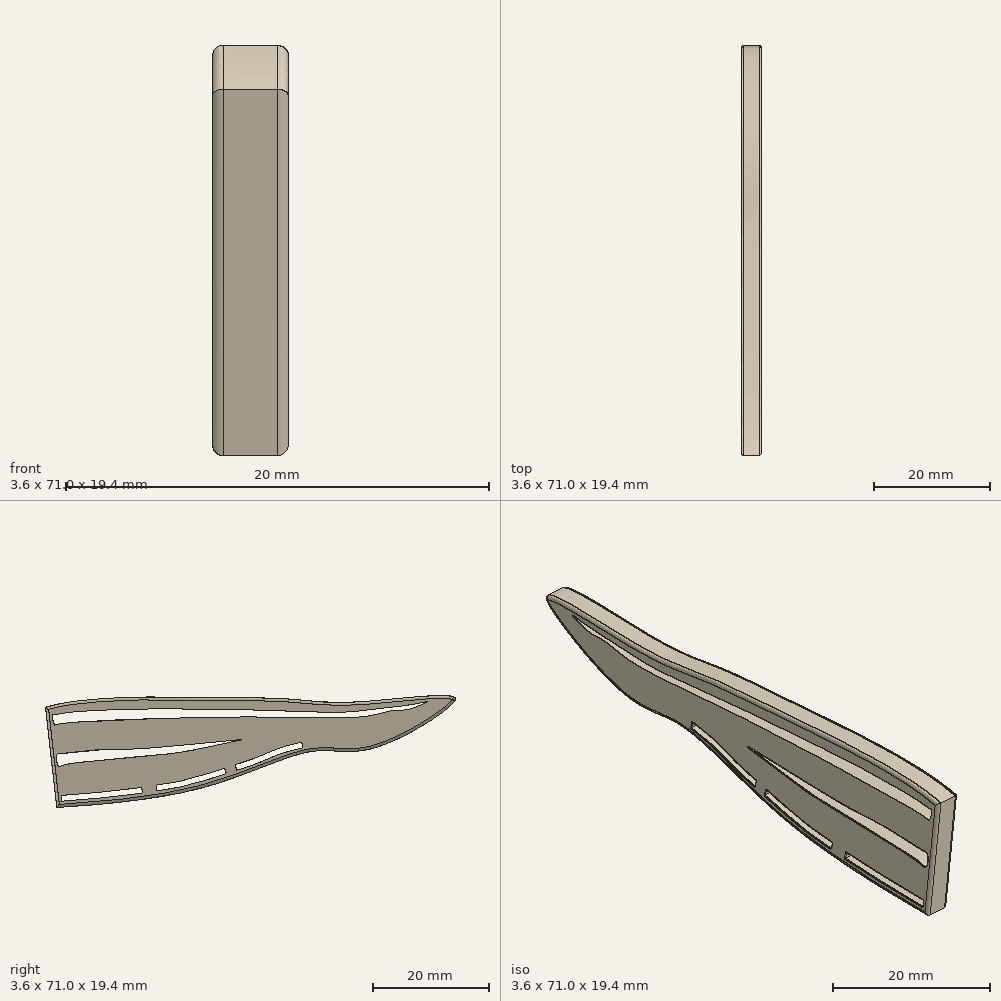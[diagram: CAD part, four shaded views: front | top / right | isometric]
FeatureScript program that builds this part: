
annotation { "Feature Type Name" : "Feature", "Feature Type Description" : "" }
export const myFeature = defineFeature(function(context is Context, id is Id, definition is map)
    precondition{}
    {
        {
            var Q0;
            Q0=qCreatedBy(makeId("Right.planeOp"),FACE);
            var sketch = newSketch(context, id + "F0", { "sketchPlane" : qUnion([Q0])});
            skFitSpline(sketch, "E0", {"points": [v(-65.8, 42.64) * mm, v(-54.6, 44.06) * mm, v(-40.36, 44.06) * mm, v(-30.2, 43.82) * mm, v(-21.14, 43.4) * mm, v(-6.78, 44.06) * mm, v(-8.12, 42.17) * mm, v(-19.19, 36.55) * mm, v(-26.3, 36.4) * mm, v(-32.36, 34.82) * mm, v(-37.4, 32.89) * mm, v(-44.89, 30.58) * mm, v(-64.17, 28.2) * mm], "startDerivative": vector(96.7, 29.58) * mm, "endDerivative": vector(-199.88, -11.49) * mm});
            skLineSegment(sketch, "E1", {"start": v(-65.8, 42.64) * mm, "end": v(-64.17, 28.2) * mm});
            skSolve(sketch);
        }
        {
            var Q0;
            Q0 = qSketchRegion(id + "F0", true);
            extrude(context, id + "F1", {"entities" : qUnion([Q0]), "depth" : 3 * mm, "offsetDistance" : 25 * mm});
        }
        {
            var Q0;
            Q0=makeQuery(id+"F1.opExtrude","SWEPT_BODY",BODY,{"disambiguationData":[OSD([sQuery(id+"F0.wireOp",EDGE,"E0"),sQuery(id+"F0.wireOp",EDGE,"E1")])]});
            var Q1;
            Q1=makeQuery(id+"F1.opExtrude","CAP_EDGE",EDGE,{"disambiguationData":[OSD([sQuery(id+"F0.wireOp",EDGE,"E1")])],"isStart":false});
            var Q2;
            {var subQ0=sQuery(id+"F0.wireOp",EDGE,"E1");var subQ1=sQuery(id+"F0.wireOp",EDGE,"E0");Q2=makeQuery(id+"F1.opExtrude","CAP_VERTEX",VERTEX,{"disambiguationData":[OSD([subQ1,subQ0]),TDD([makeQuery(id+"F0.imprint","INTERSECT",VERTEX,{"disambiguationData":[OD(1.0)],"derivedFrom":[subQ1,subQ0]})])],"isStart":false});}
            transform(context, id + "F2", {"entities" : qUnion([Q0]), "transformType" : TransformType.SCALE_UNIFORMLY, "scale" : 1.2, "scalePoint" : qUnion([Q2]), "makeCopy" : false});
        }
        {
            var Q0;
            Q0=makeQuery(id+"F1.opExtrude","CAP_FACE",FACE,{"disambiguationData":[OSD([sQuery(id+"F0.wireOp",EDGE,"E0"),sQuery(id+"F0.wireOp",EDGE,"E1")])],"isStart":true});
            var Q1;
            Q1=makeQuery(id+"F1.opExtrude","CAP_FACE",FACE,{"disambiguationData":[OSD([sQuery(id+"F0.wireOp",EDGE,"E0"),sQuery(id+"F0.wireOp",EDGE,"E1")])],"isStart":false});
            fillet(context, id + "F3", {"entities" : qUnion([Q0, Q1]), "radius" : 0.5 * mm, "tangentPropagation" : true, "allowEdgeOverflow" : false});
        }
        {
            var Q0;
            Q0=makeQuery(id+"F1.opExtrude","CAP_FACE",FACE,{"disambiguationData":[OSD([sQuery(id+"F0.wireOp",EDGE,"E0"),sQuery(id+"F0.wireOp",EDGE,"E1")])],"isStart":false});
            var sketch = newSketch(context, id + "F4", { "sketchPlane" : qUnion([Q0])});
            skFitSpline(sketch, "E2", {"points": [v(-63.36, 29.28) * mm, v(-60.8, 29.49) * mm, v(-56.8, 29.82) * mm, v(-52.19, 30.33) * mm, v(-49.34, 30.66) * mm], "startDerivative": vector(11.3, 0.95) * mm, "endDerivative": vector(11.7, 1.38) * mm});
            skFitSpline(sketch, "E3", {"points": [v(-46.81, 31.07) * mm, v(-44.13, 31.49) * mm, v(-42.5, 31.78) * mm, v(-40.28, 32.4) * mm, v(-38.2, 32.95) * mm, v(-34.8, 34.04) * mm], "startDerivative": vector(13.67, 2.17) * mm, "endDerivative": vector(14.97, 5.05) * mm});
            skFitSpline(sketch, "E4", {"points": [v(-32.97, 34.64) * mm, v(-30, 35.6) * mm, v(-27.37, 36.69) * mm, v(-25.31, 37.52) * mm, v(-23.77, 37.99) * mm, v(-21.55, 38.53) * mm], "startDerivative": vector(13.17, 3.98) * mm, "endDerivative": vector(11.96, 2.87) * mm});
            skFitSpline(sketch, "E5.0", {"points": [v(-63.45, 30.28) * mm, v(-62.98, 30.31) * mm, v(-62.27, 30.37) * mm, v(-61.25, 30.46) * mm, v(-60.15, 30.54) * mm, v(-58.63, 30.66) * mm, v(-56.65, 30.84) * mm, v(-54.9, 31.02) * mm, v(-53.57, 31.17) * mm, v(-52.62, 31.28) * mm, v(-51.75, 31.38) * mm, v(-50.68, 31.5) * mm, v(-49.95, 31.6) * mm, v(-49.46, 31.65) * mm]});
            skFitSpline(sketch, "E6.0", {"points": [v(-46.97, 32.06) * mm, v(-46.4, 32.15) * mm, v(-45.54, 32.28) * mm, v(-44.66, 32.42) * mm, v(-44.2, 32.5) * mm, v(-43.77, 32.55) * mm, v(-43.4, 32.61) * mm, v(-43.03, 32.69) * mm, v(-42.75, 32.75) * mm, v(-42.44, 32.83) * mm, v(-41.99, 32.95) * mm, v(-41.38, 33.13) * mm, v(-40.76, 33.32) * mm, v(-40.27, 33.45) * mm, v(-39.8, 33.57) * mm, v(-39.25, 33.7) * mm, v(-38.68, 33.85) * mm, v(-38.2, 34) * mm, v(-37.67, 34.15) * mm, v(-36.67, 34.47) * mm, v(-35.74, 34.78) * mm, v(-35.12, 34.99) * mm]});
            skFitSpline(sketch, "E7.0", {"points": [v(-33.26, 35.6) * mm, v(-32.71, 35.76) * mm, v(-31.9, 36) * mm, v(-30.85, 36.35) * mm, v(-29.84, 36.72) * mm, v(-28.6, 37.24) * mm, v(-27.4, 37.77) * mm, v(-26.47, 38.16) * mm, v(-25.8, 38.42) * mm, v(-25.17, 38.63) * mm, v(-24.56, 38.81) * mm, v(-23.94, 38.97) * mm, v(-23.26, 39.14) * mm, v(-22.53, 39.32) * mm, v(-22.03, 39.44) * mm, v(-21.78, 39.5) * mm]});
            skLineSegment(sketch, "E8", {"start": v(-63.36, 29.28) * mm, "end": v(-63.45, 30.28) * mm});
            skLineSegment(sketch, "E9", {"start": v(-49.34, 30.66) * mm, "end": v(-49.46, 31.65) * mm});
            skLineSegment(sketch, "E10", {"start": v(-46.81, 31.07) * mm, "end": v(-46.97, 32.06) * mm});
            skLineSegment(sketch, "E11", {"start": v(-34.8, 34.04) * mm, "end": v(-35.12, 34.99) * mm});
            skLineSegment(sketch, "E12", {"start": v(-32.97, 34.64) * mm, "end": v(-33.26, 35.6) * mm});
            skLineSegment(sketch, "E13", {"start": v(-21.55, 38.53) * mm, "end": v(-21.78, 39.5) * mm});
            skFitSpline(sketch, "E14", {"points": [v(-64.13, 37.25) * mm, v(-63.25, 37.54) * mm, v(-56.51, 38.23) * mm, v(-51.45, 38.31) * mm, v(-44.2, 38.82) * mm, v(-32.36, 39.95) * mm, v(-31.73, 39.99) * mm, v(-35.7, 39.15) * mm, v(-42.95, 37.69) * mm, v(-48.35, 37.18) * mm, v(-55.84, 36.43) * mm, v(-62.8, 35.55) * mm, v(-63.9, 35.42) * mm, v(-64.13, 37.25) * mm]});
            skFitSpline(sketch, "E15", {"points": [v(-64.66, 44.27) * mm, v(-63.12, 44.5) * mm, v(-58.15, 44.98) * mm, v(-48.5, 45.28) * mm, v(-33.88, 45.16) * mm, v(-23.46, 44.92) * mm, v(-14.46, 44.69) * mm, v(-3.69, 45.87) * mm, v(-0.9, 46.34) * mm, v(0, 46.52) * mm, v(-3.1, 45.22) * mm, v(-5.64, 45.04) * mm, v(-10.2, 44.03) * mm, v(-22.16, 43.8) * mm, v(-39.38, 43.8) * mm, v(-59.15, 43.09) * mm, v(-64.3, 42.5) * mm, v(-64.54, 42.45) * mm, v(-64.9, 44.2) * mm, v(-64.66, 44.27) * mm]});
            skSolve(sketch);
        }
        {
            var Q0;
            Q0=makeQuery(id+"F4.imprint","IMPRINT",FACE,{"disambiguationData":[TD([[makeQuery(id+"F4.imprint","IMPRINT",EDGE,{"derivedFrom":sQuery(id+"F4.wireOp",EDGE,"E2")}),1.0]])]});
            var Q1;
            Q1=makeQuery(id+"F4.imprint","IMPRINT",FACE,{"disambiguationData":[TD([[makeQuery(id+"F4.imprint","IMPRINT",EDGE,{"derivedFrom":sQuery(id+"F4.wireOp",EDGE,"E3")}),1.0]])]});
            var Q2;
            Q2=makeQuery(id+"F4.imprint","IMPRINT",FACE,{"disambiguationData":[TD([[makeQuery(id+"F4.imprint","IMPRINT",EDGE,{"derivedFrom":sQuery(id+"F4.wireOp",EDGE,"E4")}),1.0]])]});
            var Q3;
            Q3=sQuery(id+"F4.wireOp",EDGE,"a07af0f2-3b7e-4464-ae2e-b2ed8b92fa86");
            var Q4;
            Q4=sQuery(id+"F4.wireOp",EDGE,"iSIvCk0e-KTdN-Ig7o-GTeZ-tfcoK67rNe0M");
            extrude(context, id + "F5", {"entities" : qUnion([Q0, Q1, Q2]), "operationType" : NewBodyOperationType.REMOVE, "surfaceEntities" : qUnion([Q3, Q4]), "oppositeDirection" : true, "depth" : 25 * mm, "offsetDistance" : 25 * mm});
        }
        {
            var Q0;
            Q0 = qSketchRegion(id + "F4", true);
            extrude(context, id + "F6", {"entities" : qUnion([Q0]), "operationType" : NewBodyOperationType.REMOVE, "oppositeDirection" : true, "depth" : 25 * mm, "offsetDistance" : 25 * mm});
        }
        {
            var Q0;
            Q0=makeQuery(id+"F6.boolean.opBoolean","COPY",EDGE,{"derivedFrom":makeQuery(id+"F6.opExtrude","CAP_EDGE",EDGE,{"disambiguationData":[OSD([sQuery(id+"F4.wireOp",EDGE,"E14")])],"isStart":true})});
            var Q1;
            Q1=makeQuery(id+"F5.boolean.opBoolean","COPY",EDGE,{"derivedFrom":makeQuery(id+"F5.opExtrude","CAP_EDGE",EDGE,{"disambiguationData":[OSD([sQuery(id+"F4.wireOp",EDGE,"E2")])],"isStart":true})});
            var Q2;
            Q2=makeQuery(id+"F5.boolean.opBoolean","COPY",EDGE,{"derivedFrom":makeQuery(id+"F5.opExtrude","CAP_EDGE",EDGE,{"disambiguationData":[OSD([sQuery(id+"F4.wireOp",EDGE,"E5.0")])],"isStart":true})});
            var Q3;
            Q3=makeQuery(id+"F5.boolean.opBoolean","COPY",EDGE,{"derivedFrom":makeQuery(id+"F5.opExtrude","CAP_EDGE",EDGE,{"disambiguationData":[OSD([sQuery(id+"F4.wireOp",EDGE,"E9")])],"isStart":true})});
            var Q4;
            Q4=makeQuery(id+"F5.boolean.opBoolean","COPY",EDGE,{"derivedFrom":makeQuery(id+"F5.opExtrude","CAP_EDGE",EDGE,{"disambiguationData":[OSD([sQuery(id+"F4.wireOp",EDGE,"E8")])],"isStart":true})});
            var Q5;
            Q5=makeQuery(id+"F5.boolean.opBoolean","COPY",EDGE,{"derivedFrom":makeQuery(id+"F5.opExtrude","CAP_EDGE",EDGE,{"disambiguationData":[OSD([sQuery(id+"F4.wireOp",EDGE,"E6.0")])],"isStart":true})});
            var Q6;
            Q6=makeQuery(id+"F5.boolean.opBoolean","COPY",EDGE,{"derivedFrom":makeQuery(id+"F5.opExtrude","CAP_EDGE",EDGE,{"disambiguationData":[OSD([sQuery(id+"F4.wireOp",EDGE,"E3")])],"isStart":true})});
            var Q7;
            Q7=makeQuery(id+"F5.boolean.opBoolean","COPY",EDGE,{"derivedFrom":makeQuery(id+"F5.opExtrude","CAP_EDGE",EDGE,{"disambiguationData":[OSD([sQuery(id+"F4.wireOp",EDGE,"E11")])],"isStart":true})});
            var Q8;
            Q8=makeQuery(id+"F5.boolean.opBoolean","COPY",EDGE,{"derivedFrom":makeQuery(id+"F5.opExtrude","CAP_EDGE",EDGE,{"disambiguationData":[OSD([sQuery(id+"F4.wireOp",EDGE,"E10")])],"isStart":true})});
            var Q9;
            Q9=makeQuery(id+"F5.boolean.opBoolean","COPY",EDGE,{"derivedFrom":makeQuery(id+"F5.opExtrude","CAP_EDGE",EDGE,{"disambiguationData":[OSD([sQuery(id+"F4.wireOp",EDGE,"E7.0")])],"isStart":true})});
            var Q10;
            Q10=makeQuery(id+"F5.boolean.opBoolean","COPY",EDGE,{"derivedFrom":makeQuery(id+"F5.opExtrude","CAP_EDGE",EDGE,{"disambiguationData":[OSD([sQuery(id+"F4.wireOp",EDGE,"E4")])],"isStart":true})});
            var Q11;
            Q11=makeQuery(id+"F5.boolean.opBoolean","COPY",EDGE,{"derivedFrom":makeQuery(id+"F5.opExtrude","CAP_EDGE",EDGE,{"disambiguationData":[OSD([sQuery(id+"F4.wireOp",EDGE,"E12")])],"isStart":true})});
            var Q12;
            Q12=makeQuery(id+"F5.boolean.opBoolean","COPY",EDGE,{"derivedFrom":makeQuery(id+"F5.opExtrude","CAP_EDGE",EDGE,{"disambiguationData":[OSD([sQuery(id+"F4.wireOp",EDGE,"E13")])],"isStart":true})});
            var Q13;
            Q13=makeQuery(id+"F6.boolean.opBoolean","INTERSECT",EDGE,{"derivedFrom":[makeQuery(id+"F1.opExtrude","CAP_FACE",FACE,{"disambiguationData":[OSD([sQuery(id+"F0.wireOp",EDGE,"E0"),sQuery(id+"F0.wireOp",EDGE,"E1")])],"isStart":true}),makeQuery(id+"F6.opExtrude","SWEPT_FACE",FACE,{"disambiguationData":[OSD([sQuery(id+"F4.wireOp",EDGE,"E14")])]})]});
            var Q14;
            Q14=makeQuery(id+"F5.boolean.opBoolean","INTERSECT",EDGE,{"derivedFrom":[makeQuery(id+"F1.opExtrude","CAP_FACE",FACE,{"disambiguationData":[OSD([sQuery(id+"F0.wireOp",EDGE,"E0"),sQuery(id+"F0.wireOp",EDGE,"E1")])],"isStart":true}),makeQuery(id+"F5.opExtrude","SWEPT_FACE",FACE,{"disambiguationData":[OSD([sQuery(id+"F4.wireOp",EDGE,"E5.0")])]})]});
            var Q15;
            Q15=makeQuery(id+"F5.boolean.opBoolean","INTERSECT",EDGE,{"derivedFrom":[makeQuery(id+"F1.opExtrude","CAP_FACE",FACE,{"disambiguationData":[OSD([sQuery(id+"F0.wireOp",EDGE,"E0"),sQuery(id+"F0.wireOp",EDGE,"E1")])],"isStart":true}),makeQuery(id+"F5.opExtrude","SWEPT_FACE",FACE,{"disambiguationData":[OSD([sQuery(id+"F4.wireOp",EDGE,"E6.0")])]})]});
            var Q16;
            Q16=makeQuery(id+"F5.boolean.opBoolean","INTERSECT",EDGE,{"derivedFrom":[makeQuery(id+"F1.opExtrude","CAP_FACE",FACE,{"disambiguationData":[OSD([sQuery(id+"F0.wireOp",EDGE,"E0"),sQuery(id+"F0.wireOp",EDGE,"E1")])],"isStart":true}),makeQuery(id+"F5.opExtrude","SWEPT_FACE",FACE,{"disambiguationData":[OSD([sQuery(id+"F4.wireOp",EDGE,"E7.0")])]})]});
            var Q17;
            Q17=makeQuery(id+"F5.boolean.opBoolean","INTERSECT",EDGE,{"derivedFrom":[makeQuery(id+"F1.opExtrude","CAP_FACE",FACE,{"disambiguationData":[OSD([sQuery(id+"F0.wireOp",EDGE,"E0"),sQuery(id+"F0.wireOp",EDGE,"E1")])],"isStart":true}),makeQuery(id+"F5.opExtrude","SWEPT_FACE",FACE,{"disambiguationData":[OSD([sQuery(id+"F4.wireOp",EDGE,"E8")])]})]});
            var Q18;
            Q18=makeQuery(id+"F5.boolean.opBoolean","INTERSECT",EDGE,{"derivedFrom":[makeQuery(id+"F1.opExtrude","CAP_FACE",FACE,{"disambiguationData":[OSD([sQuery(id+"F0.wireOp",EDGE,"E0"),sQuery(id+"F0.wireOp",EDGE,"E1")])],"isStart":true}),makeQuery(id+"F5.opExtrude","SWEPT_FACE",FACE,{"disambiguationData":[OSD([sQuery(id+"F4.wireOp",EDGE,"E2")])]})]});
            var Q19;
            Q19=makeQuery(id+"F5.boolean.opBoolean","INTERSECT",EDGE,{"derivedFrom":[makeQuery(id+"F1.opExtrude","CAP_FACE",FACE,{"disambiguationData":[OSD([sQuery(id+"F0.wireOp",EDGE,"E0"),sQuery(id+"F0.wireOp",EDGE,"E1")])],"isStart":true}),makeQuery(id+"F5.opExtrude","SWEPT_FACE",FACE,{"disambiguationData":[OSD([sQuery(id+"F4.wireOp",EDGE,"E9")])]})]});
            var Q20;
            Q20=makeQuery(id+"F5.boolean.opBoolean","INTERSECT",EDGE,{"derivedFrom":[makeQuery(id+"F1.opExtrude","CAP_FACE",FACE,{"disambiguationData":[OSD([sQuery(id+"F0.wireOp",EDGE,"E0"),sQuery(id+"F0.wireOp",EDGE,"E1")])],"isStart":true}),makeQuery(id+"F5.opExtrude","SWEPT_FACE",FACE,{"disambiguationData":[OSD([sQuery(id+"F4.wireOp",EDGE,"E10")])]})]});
            var Q21;
            Q21=makeQuery(id+"F5.boolean.opBoolean","INTERSECT",EDGE,{"derivedFrom":[makeQuery(id+"F1.opExtrude","CAP_FACE",FACE,{"disambiguationData":[OSD([sQuery(id+"F0.wireOp",EDGE,"E0"),sQuery(id+"F0.wireOp",EDGE,"E1")])],"isStart":true}),makeQuery(id+"F5.opExtrude","SWEPT_FACE",FACE,{"disambiguationData":[OSD([sQuery(id+"F4.wireOp",EDGE,"E3")])]})]});
            var Q22;
            Q22=makeQuery(id+"F5.boolean.opBoolean","INTERSECT",EDGE,{"derivedFrom":[makeQuery(id+"F1.opExtrude","CAP_FACE",FACE,{"disambiguationData":[OSD([sQuery(id+"F0.wireOp",EDGE,"E0"),sQuery(id+"F0.wireOp",EDGE,"E1")])],"isStart":true}),makeQuery(id+"F5.opExtrude","SWEPT_FACE",FACE,{"disambiguationData":[OSD([sQuery(id+"F4.wireOp",EDGE,"E11")])]})]});
            var Q23;
            Q23=makeQuery(id+"F5.boolean.opBoolean","INTERSECT",EDGE,{"derivedFrom":[makeQuery(id+"F1.opExtrude","CAP_FACE",FACE,{"disambiguationData":[OSD([sQuery(id+"F0.wireOp",EDGE,"E0"),sQuery(id+"F0.wireOp",EDGE,"E1")])],"isStart":true}),makeQuery(id+"F5.opExtrude","SWEPT_FACE",FACE,{"disambiguationData":[OSD([sQuery(id+"F4.wireOp",EDGE,"E4")])]})]});
            var Q24;
            Q24=makeQuery(id+"F5.boolean.opBoolean","INTERSECT",EDGE,{"derivedFrom":[makeQuery(id+"F1.opExtrude","CAP_FACE",FACE,{"disambiguationData":[OSD([sQuery(id+"F0.wireOp",EDGE,"E0"),sQuery(id+"F0.wireOp",EDGE,"E1")])],"isStart":true}),makeQuery(id+"F5.opExtrude","SWEPT_FACE",FACE,{"disambiguationData":[OSD([sQuery(id+"F4.wireOp",EDGE,"E12")])]})]});
            var Q25;
            Q25=makeQuery(id+"F5.boolean.opBoolean","INTERSECT",EDGE,{"derivedFrom":[makeQuery(id+"F1.opExtrude","CAP_FACE",FACE,{"disambiguationData":[OSD([sQuery(id+"F0.wireOp",EDGE,"E0"),sQuery(id+"F0.wireOp",EDGE,"E1")])],"isStart":true}),makeQuery(id+"F5.opExtrude","SWEPT_FACE",FACE,{"disambiguationData":[OSD([sQuery(id+"F4.wireOp",EDGE,"E13")])]})]});
            fillet(context, id + "F7", {"entities" : qUnion([Q0, Q1, Q2, Q3, Q4, Q5, Q6, Q7, Q8, Q9, Q10, Q11, Q12, Q13, Q14, Q15, Q16, Q17, Q18, Q19, Q20, Q21, Q22, Q23, Q24, Q25]), "radius" : 0.1 * mm, "tangentPropagation" : true, "allowEdgeOverflow" : false});
        }
    });
